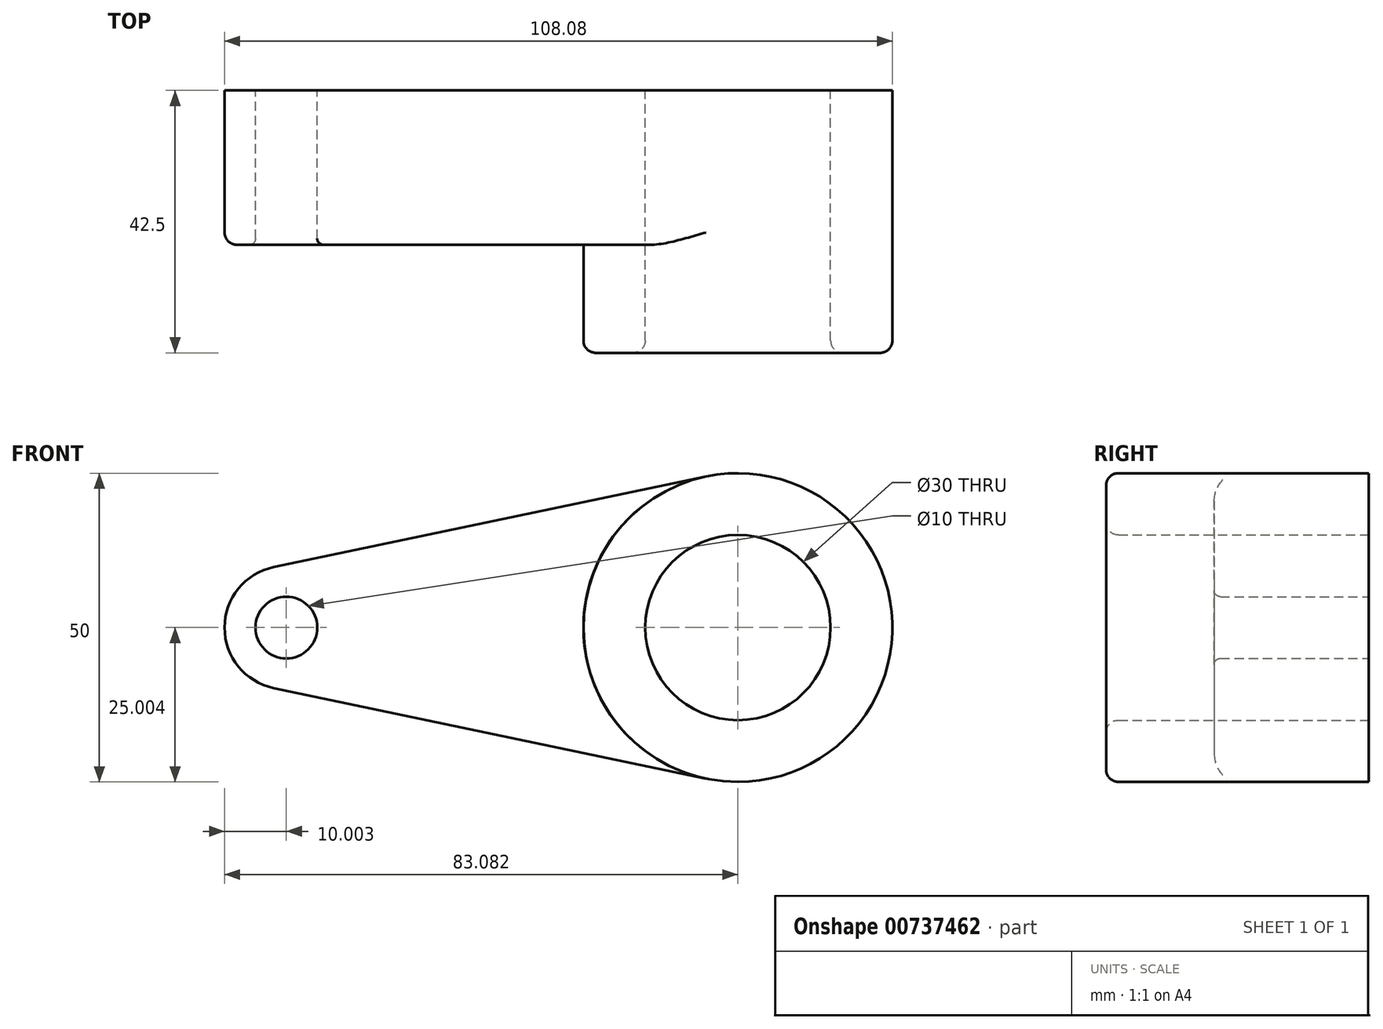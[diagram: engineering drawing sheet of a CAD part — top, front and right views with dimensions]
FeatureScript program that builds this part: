
annotation { "Feature Type Name" : "Feature", "Feature Type Description" : "" }
export const myFeature = defineFeature(function(context is Context, id is Id, definition is map)
    precondition{}
    {
        {
            var Q0;
            Q0=qCreatedBy(makeId("Front.planeOp"),FACE);
            var sketch = newSketch(context, id + "F0", { "sketchPlane" : qUnion([Q0])});
            skCircle(sketch, "E0", {"center": v(-58.03, 7.48) * mm, "radius": 10 * mm});
            skCircle(sketch, "E1", {"center": v(15.05, 7.48) * mm, "radius": 25 * mm});
            skLineSegment(sketch, "E2", {"start": v(-60.08, 17.27) * mm, "end": v(9.92, 31.95) * mm});
            skLineSegment(sketch, "E3", {"start": v(-58.03, 7.48) * mm, "end": v(15.05, 7.48) * mm, "construction": true});
            skLineSegment(sketch, "E4.MirrorCS", {"start": v(-60.08, -2.3) * mm, "end": v(9.92, -16.98) * mm});
            skCircle(sketch, "E5", {"center": v(-58.03, 7.48) * mm, "radius": 5 * mm});
            skCircle(sketch, "E6", {"center": v(15.05, 7.48) * mm, "radius": 15 * mm});
            skSolve(sketch);
        }
        {
            var Q0;
            {var subQ0=sQuery(id+"F0.wireOp",EDGE,"E2");Q0=makeQuery(id+"F0.imprint","IMPRINT",FACE,{"disambiguationData":[TD([[makeQuery(id+"F0.imprint","IMPRINT",EDGE,{"derivedFrom":subQ0}),-1.0]])]});}
            var Q1;
            Q1=makeQuery(id+"F0.imprint","IMPRINT",FACE,{"disambiguationData":[TD([[makeQuery(id+"F0.imprint","IMPRINT",EDGE,{"derivedFrom":sQuery(id+"F0.wireOp",EDGE,"E6")}),-1.0]])]});
            var Q2;
            Q2=makeQuery(id+"F0.imprint","IMPRINT",FACE,{"disambiguationData":[TD([[makeQuery(id+"F0.imprint","IMPRINT",EDGE,{"derivedFrom":sQuery(id+"F0.wireOp",EDGE,"E5")}),-1.0]])]});
            extrude(context, id + "F1", {"entities" : qUnion([Q0, Q1, Q2]), "depth" : 25 * mm, "offsetDistance" : 25 * mm, "symmetric" : true});
        }
        {
            var Q0;
            Q0=makeQuery(id+"F0.imprint","IMPRINT",FACE,{"disambiguationData":[TD([[makeQuery(id+"F0.imprint","IMPRINT",EDGE,{"derivedFrom":sQuery(id+"F0.wireOp",EDGE,"E6")}),-1.0]])]});
            extrude(context, id + "F2", {"entities" : qUnion([Q0]), "operationType" : NewBodyOperationType.ADD, "depth" : 30 * mm, "offsetDistance" : 25 * mm});
        }
        {
            var Q0;
            Q0=makeQuery(id+"F1.opExtrude","CAP_EDGE",EDGE,{"disambiguationData":[OSD([sQuery(id+"F0.wireOp",EDGE,"E4.MirrorCS")])],"isStart":false});
            var Q1;
            Q1=makeQuery(id+"F1.opExtrude","CAP_EDGE",EDGE,{"disambiguationData":[OSD([sQuery(id+"F0.wireOp",EDGE,"E0")])],"isStart":false});
            var Q2;
            Q2=makeQuery(id+"F1.opExtrude","CAP_EDGE",EDGE,{"disambiguationData":[OSD([sQuery(id+"F0.wireOp",EDGE,"E2")])],"isStart":false});
            var Q3;
            Q3=makeQuery(id+"F2.opExtrude","CAP_EDGE",EDGE,{"disambiguationData":[OSD([sQuery(id+"F0.wireOp",EDGE,"E1")])],"isStart":false});
            var Q4;
            Q4=makeQuery(id+"F2.opExtrude","CAP_EDGE",EDGE,{"disambiguationData":[OSD([sQuery(id+"F0.wireOp",EDGE,"E6")])],"isStart":false});
            fillet(context, id + "F3", {"entities" : qUnion([Q0, Q1, Q2, Q3, Q4]), "radius" : 2 * mm, "allowEdgeOverflow" : false});
        }
        {
            var Q0;
            Q0=makeQuery(id+"F1.opExtrude","CAP_EDGE",EDGE,{"disambiguationData":[OSD([sQuery(id+"F0.wireOp",EDGE,"E5")])],"isStart":false});
            fillet(context, id + "F4", {"entities" : qUnion([Q0]), "radius" : 1 * mm, "tangentPropagation" : true, "allowEdgeOverflow" : false});
        }
    });
